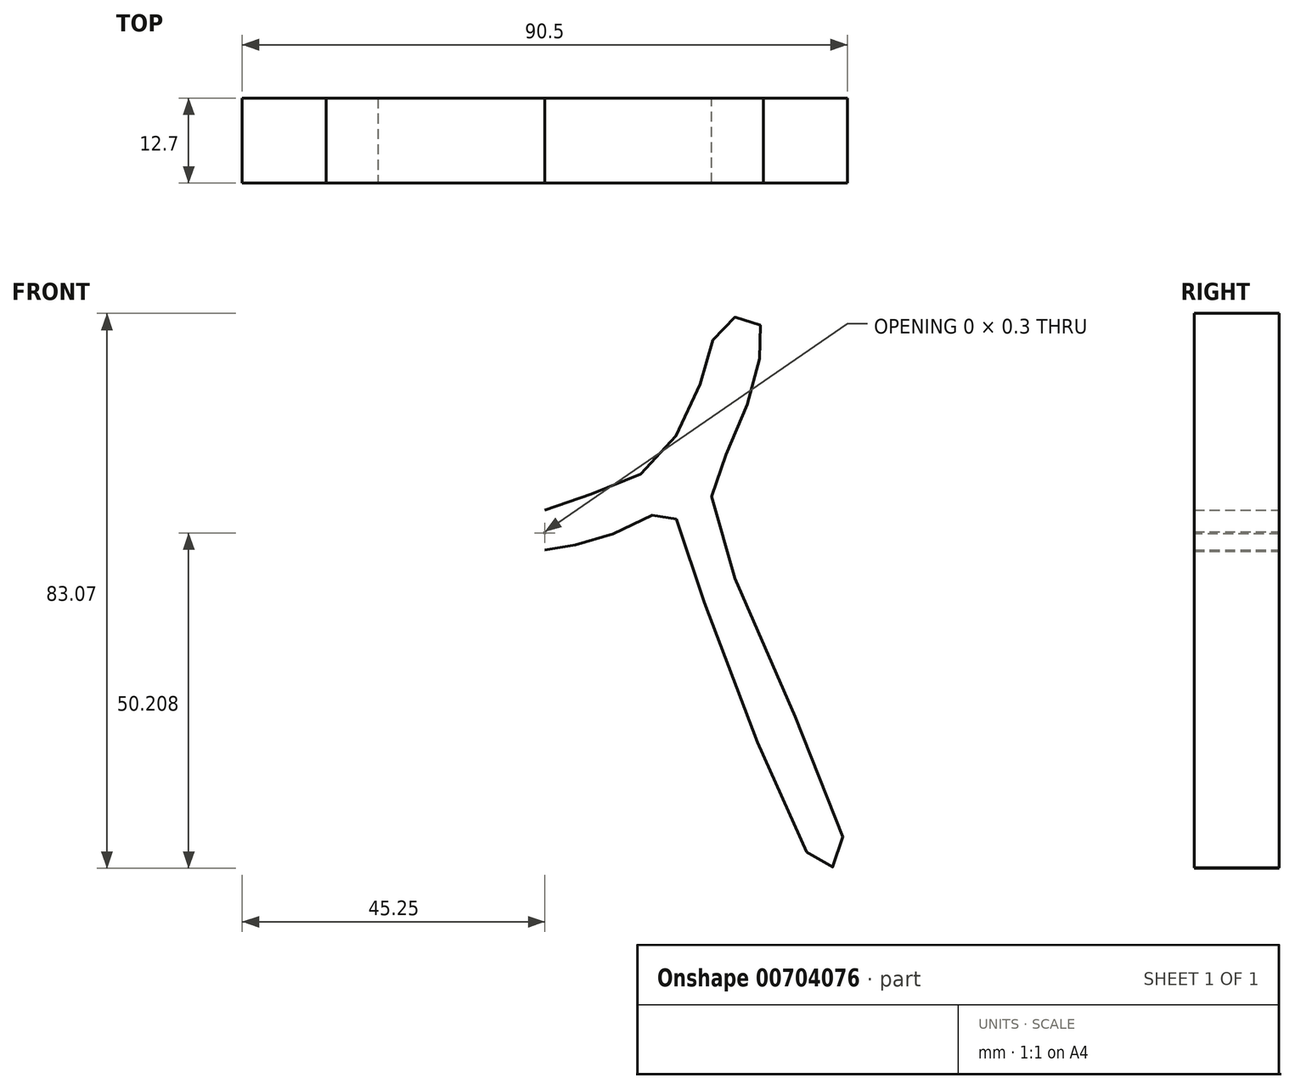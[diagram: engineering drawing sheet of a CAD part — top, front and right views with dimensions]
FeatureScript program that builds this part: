
annotation { "Feature Type Name" : "Feature", "Feature Type Description" : "" }
export const myFeature = defineFeature(function(context is Context, id is Id, definition is map)
    precondition{}
    {
        {
            var Q0;
            Q0=qCreatedBy(makeId("Front.planeOp"),FACE);
            var sketch = newSketch(context, id + "F0", { "sketchPlane" : qUnion([Q0])});
            skFitSpline(sketch, "E0", {"points": [v(0, 0) * mm, v(8.91, 2.88) * mm, v(16.69, 7.44) * mm, v(22.58, 16.82) * mm, v(25, 25.13) * mm, v(27.14, 27.8) * mm, v(30.09, 29.42) * mm, v(32.5, 27) * mm, v(32.23, 22.98) * mm, v(30.09, 15.21) * mm, v(26.07, 6.1) * mm, v(26.07, -3.82) * mm, v(45.1, -53.14) * mm, v(42.42, -53.4) * mm, v(40.8, -53.4) * mm, v(20.97, -5.43) * mm, v(18.3, 0) * mm, v(13.47, -2.21) * mm, v(7.84, -4.36) * mm, v(2.75, -5.7) * mm, v(0, -5.96) * mm, v(0, -3.28) * mm, v(0, 0) * mm]});
            skSolve(sketch);
        }
        {
            var Q0;
            Q0=makeQuery(id+"F0.imprint","IMPRINT",FACE,{"disambiguationData":[TD([[makeQuery(id+"F0.imprint","IMPRINT",EDGE,{"derivedFrom":sQuery(id+"F0.wireOp",EDGE,"E0")}),-1.0]])]});
            extrude(context, id + "F1", {"entities" : qUnion([Q0]), "depth" : 12.7 * mm, "offsetDistance" : 25.4 * mm});
        }
        {
            var Q0;
            Q0=makeQuery(id+"F1.opExtrude","SWEPT_BODY",BODY,{"disambiguationData":[OSD([sQuery(id+"F0.wireOp",EDGE,"E0")])]});
            var Q1;
            Q1=qCreatedBy(makeId("Right.planeOp"),FACE);
            mirror(context, id + "F2", {"operationType" : NewBodyOperationType.ADD, "entities" : qUnion([Q0]), "mirrorPlane" : qUnion([Q1])});
        }
    });
